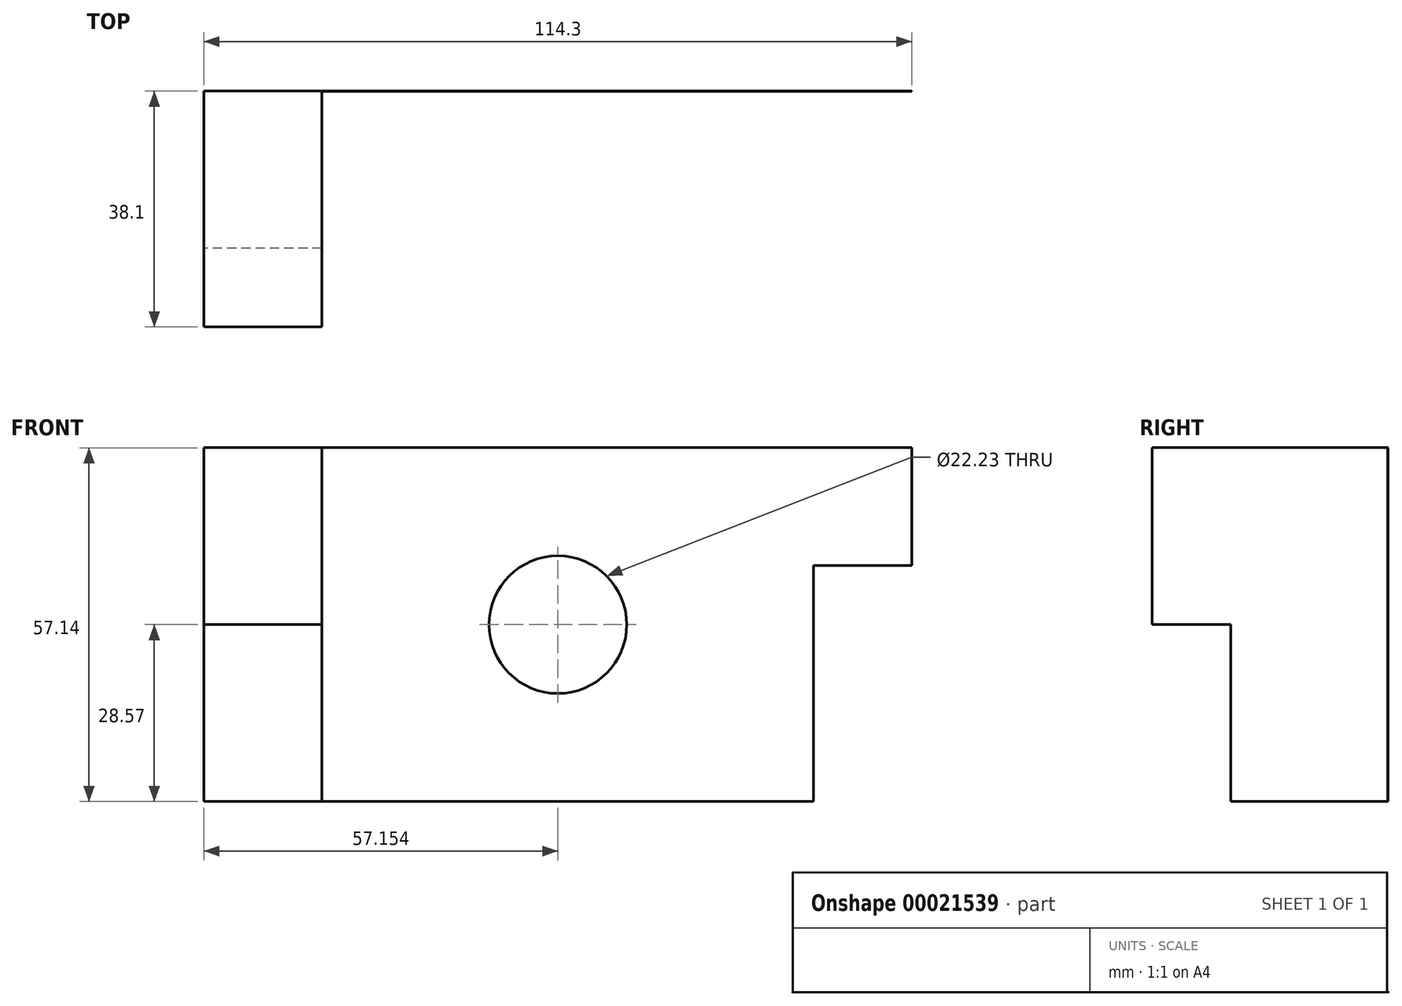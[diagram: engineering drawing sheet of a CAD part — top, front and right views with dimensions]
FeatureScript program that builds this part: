
annotation { "Feature Type Name" : "Feature", "Feature Type Description" : "" }
export const myFeature = defineFeature(function(context is Context, id is Id, definition is map)
    precondition{}
    {
        {
            var Q0;
            Q0=qCreatedBy(makeId("Front.planeOp"),FACE);
            var sketch = newSketch(context, id + "F0", { "sketchPlane" : qUnion([Q0])});
            skLineSegment(sketch, "E0.bottom", {"start": v(-64.1, 28.58) * mm, "end": v(31.15, 28.58) * mm});
            skLineSegment(sketch, "E0.top", {"start": v(-64.1, -28.58) * mm, "end": v(31.15, -28.58) * mm});
            skLineSegment(sketch, "E0.left", {"start": v(-64.1, 28.58) * mm, "end": v(-64.1, -28.58) * mm});
            skLineSegment(sketch, "E0.right", {"start": v(31.15, 28.58) * mm, "end": v(31.15, -28.58) * mm});
            skLineSegment(sketch, "E1.bottom", {"start": v(15.28, 9.52) * mm, "end": v(31.15, 9.52) * mm});
            skLineSegment(sketch, "E1.top", {"start": v(15.28, -28.58) * mm, "end": v(31.15, -28.58) * mm});
            skLineSegment(sketch, "E1.left", {"start": v(15.28, 9.52) * mm, "end": v(15.28, -28.58) * mm});
            skLineSegment(sketch, "E1.right", {"start": v(31.15, 9.52) * mm, "end": v(31.15, -28.58) * mm});
            skCircle(sketch, "E2", {"center": v(-26, 0) * mm, "radius": 11.11 * mm});
            skSolve(sketch);
        }
        {
            var Q0;
            Q0=makeQuery(id+"F0.imprint","IMPRINT",FACE,{"disambiguationData":[TD([[makeQuery(id+"F0.imprint","IMPRINT",EDGE,{"derivedFrom":sQuery(id+"F0.wireOp",EDGE,"E0.bottom")}),-1.0]])]});
            extrude(context, id + "F1", {"entities" : qUnion([Q0]), "depth" : 3 / 101.6 * mm});
        }
        {
            var Q0;
            Q0=qCreatedBy(makeId("Front.planeOp"),FACE);
            var sketch = newSketch(context, id + "F2", { "sketchPlane" : qUnion([Q0])});
            skLineSegment(sketch, "E3.bottom", {"start": v(-64.1, 0) * mm, "end": v(-83.15, 0) * mm});
            skLineSegment(sketch, "E3.top", {"start": v(-64.1, -28.58) * mm, "end": v(-83.15, -28.58) * mm});
            skLineSegment(sketch, "E3.left", {"start": v(-64.1, 0) * mm, "end": v(-64.1, -28.58) * mm});
            skLineSegment(sketch, "E3.right", {"start": v(-83.15, 0) * mm, "end": v(-83.15, -28.58) * mm});
            skSolve(sketch);
        }
        {
            var Q0;
            Q0=qCreatedBy(makeId("Front.planeOp"),FACE);
            var sketch = newSketch(context, id + "F3", { "sketchPlane" : qUnion([Q0])});
            skLineSegment(sketch, "E4.bottom", {"start": v(-64.1, 28.58) * mm, "end": v(-83.15, 28.58) * mm});
            skLineSegment(sketch, "E4.top", {"start": v(-64.1, 0) * mm, "end": v(-83.15, 0) * mm});
            skLineSegment(sketch, "E4.left", {"start": v(-64.1, 28.58) * mm, "end": v(-64.1, 0) * mm});
            skLineSegment(sketch, "E4.right", {"start": v(-83.15, 28.58) * mm, "end": v(-83.15, 0) * mm});
            skSolve(sketch);
        }
        {
            var Q0;
            Q0=makeQuery(id+"F2.imprint","IMPRINT",FACE,{"disambiguationData":[TD([[makeQuery(id+"F2.imprint","IMPRINT",EDGE,{"derivedFrom":sQuery(id+"F2.wireOp",EDGE,"E3.bottom")}),1.0]])]});
            extrude(context, id + "F4", {"entities" : qUnion([Q0]), "operationType" : NewBodyOperationType.ADD, "depth" : 25.4 * mm});
        }
        {
            var Q0;
            Q0 = qSketchRegion(id + "F3", true);
            extrude(context, id + "F5", {"entities" : qUnion([Q0]), "operationType" : NewBodyOperationType.ADD, "depth" : 38.1 * mm});
        }
    });
